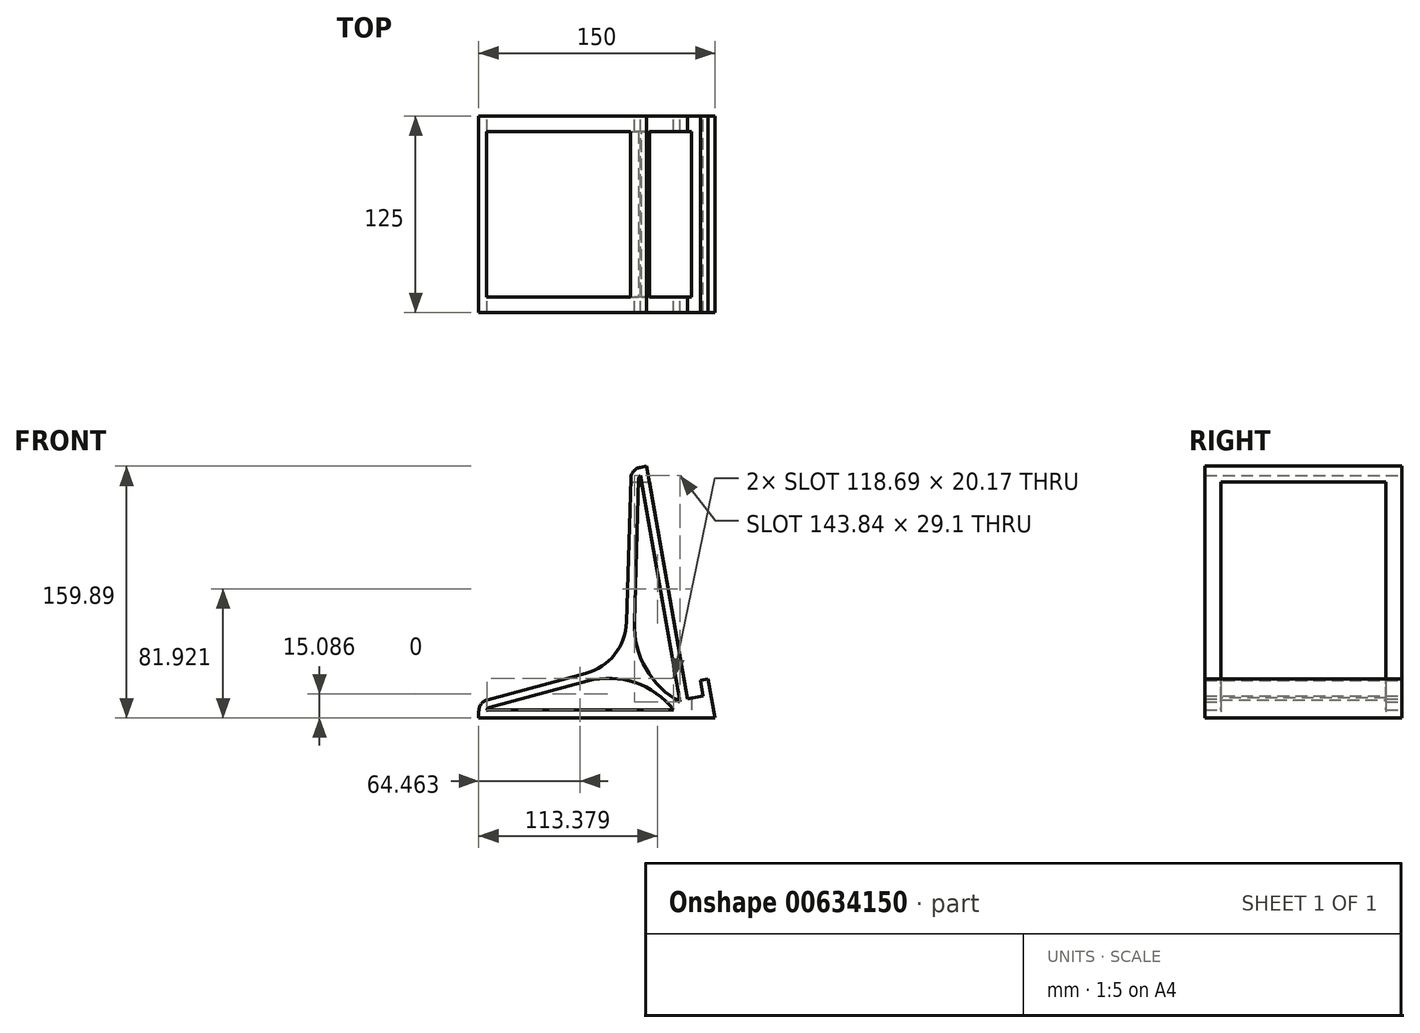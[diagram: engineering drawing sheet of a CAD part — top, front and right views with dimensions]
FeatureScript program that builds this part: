
annotation { "Feature Type Name" : "Feature", "Feature Type Description" : "" }
export const myFeature = defineFeature(function(context is Context, id is Id, definition is map)
    precondition{}
    {
        {
            var Q0;
            Q0=qCreatedBy(makeId("Front.planeOp"),FACE);
            var sketch = newSketch(context, id + "F0", { "sketchPlane" : qUnion([Q0])});
            skLineSegment(sketch, "E0", {"start": v(0, 0) * mm, "end": v(-150, 0) * mm});
            skLineSegment(sketch, "E1", {"start": v(-150, 0) * mm, "end": v(-150, 4.25) * mm});
            skLineSegment(sketch, "E2", {"start": v(-144.45, 11.5) * mm, "end": v(-82.07, 28.25) * mm});
            skLineSegment(sketch, "E3", {"start": v(-56.17, 61) * mm, "end": v(-53.45, 152.05) * mm});
            skLineSegment(sketch, "E4", {"start": v(-47.26, 159.21) * mm, "end": v(-43.42, 159.89) * mm});
            skLineSegment(sketch, "E5", {"start": v(-43.42, 159.89) * mm, "end": v(-17.38, 12.17) * mm});
            skLineSegment(sketch, "E6", {"start": v(-17.38, 12.17) * mm, "end": v(-7.53, 13.9) * mm});
            skLineSegment(sketch, "E7", {"start": v(-7.53, 13.9) * mm, "end": v(-9.27, 23.75) * mm});
            skLineSegment(sketch, "E8", {"start": v(-9.27, 23.75) * mm, "end": v(-4.34, 24.62) * mm});
            skLineSegment(sketch, "E9", {"start": v(-4.34, 24.62) * mm, "end": v(0, 0) * mm});
            skPoint(sketch, "E10.visualSharp", {"position": v(-150, 10) * mm});
            skArc(sketch, "E10.filletArc", {"start": v(-144.45, 11.5) * mm, "mid": v(-148.45, 8.81) * mm, "end": v(-150, 4.25) * mm});
            skPoint(sketch, "E11.visualSharp", {"position": v(-53.27, 158.15) * mm});
            skArc(sketch, "E11.filletArc", {"start": v(-47.26, 159.21) * mm, "mid": v(-51.63, 156.73) * mm, "end": v(-53.45, 152.05) * mm});
            skPoint(sketch, "E12.visualSharp", {"position": v(-56.94, 35) * mm});
            skArc(sketch, "E12.filletArc", {"start": v(-82.07, 28.25) * mm, "mid": v(-63.7, 40.34) * mm, "end": v(-56.17, 61) * mm});
            skLineSegment(sketch, "E13.0", {"start": v(-47.44, 153.84) * mm, "end": v(-21.2, 5) * mm});
            skArc(sketch, "E13.1", {"start": v(-47.44, 153.84) * mm, "mid": v(-48.17, 152.99) * mm, "end": v(-48.46, 151.9) * mm});
            skLineSegment(sketch, "E13.2", {"start": v(-51.17, 60.86) * mm, "end": v(-48.46, 151.9) * mm});
            skArc(sketch, "E13.4", {"start": v(-143.15, 6.66) * mm, "mid": v(-144.23, 6.05) * mm, "end": v(-144.88, 5) * mm});
            skLineSegment(sketch, "E13.5", {"start": v(-143.15, 6.66) * mm, "end": v(-80.77, 23.42) * mm});
            skArc(sketch, "E13.6", {"start": v(-80.77, 23.42) * mm, "mid": v(-59.78, 37.24) * mm, "end": v(-51.17, 60.86) * mm});
            skLineSegment(sketch, "E14.trimOffspring", {"start": v(-21.2, 5) * mm, "end": v(-144.88, 5) * mm});
            skArc(sketch, "E15", {"start": v(-26.2, 5) * mm, "mid": v(-50.7, 22.47) * mm, "end": v(-80.77, 23.42) * mm});
            skArc(sketch, "E16", {"start": v(-51.17, 60.86) * mm, "mid": v(-43.79, 31.33) * mm, "end": v(-22.07, 10) * mm});
            skSolve(sketch);
        }
        {
            var Q0;
            Q0 = qSketchRegion(id + "F0", true);
            var Q1;
            Q1=makeQuery(id+"F0.imprint","IMPRINT",FACE,{"disambiguationData":[TD([[makeQuery(id+"F0.imprint","IMPRINT",EDGE,{"derivedFrom":sQuery(id+"F0.wireOp",EDGE,"E13.6")}),-1.0]])]});
            extrude(context, id + "F1", {"entities" : qUnion([Q0, Q1]), "depth" : 125 * mm, "offsetDistance" : 25 * mm});
        }
        {
            var Q0;
            Q0=makeQuery(id+"F1.opExtrude","SWEPT_FACE",FACE,{"disambiguationData":[OSD([sQuery(id+"F0.wireOp",EDGE,"E0")])]});
            var sketch = newSketch(context, id + "F2", { "sketchPlane" : qUnion([Q0])});
            skLineSegment(sketch, "E17.bottom", {"start": v(-145, 115) * mm, "end": v(-15, 115) * mm});
            skLineSegment(sketch, "E17.top", {"start": v(-145, 10) * mm, "end": v(-15, 10) * mm});
            skLineSegment(sketch, "E17.left", {"start": v(-145, 115) * mm, "end": v(-145, 10) * mm});
            skLineSegment(sketch, "E17.right", {"start": v(-15, 115) * mm, "end": v(-15, 10) * mm});
            skSolve(sketch);
        }
        {
            var Q0;
            Q0 = qSketchRegion(id + "F2", true);
            extrude(context, id + "F3", {"entities" : qUnion([Q0]), "operationType" : NewBodyOperationType.REMOVE, "oppositeDirection" : true, "depth" : 150 * mm, "offsetDistance" : 25 * mm});
        }
    });
